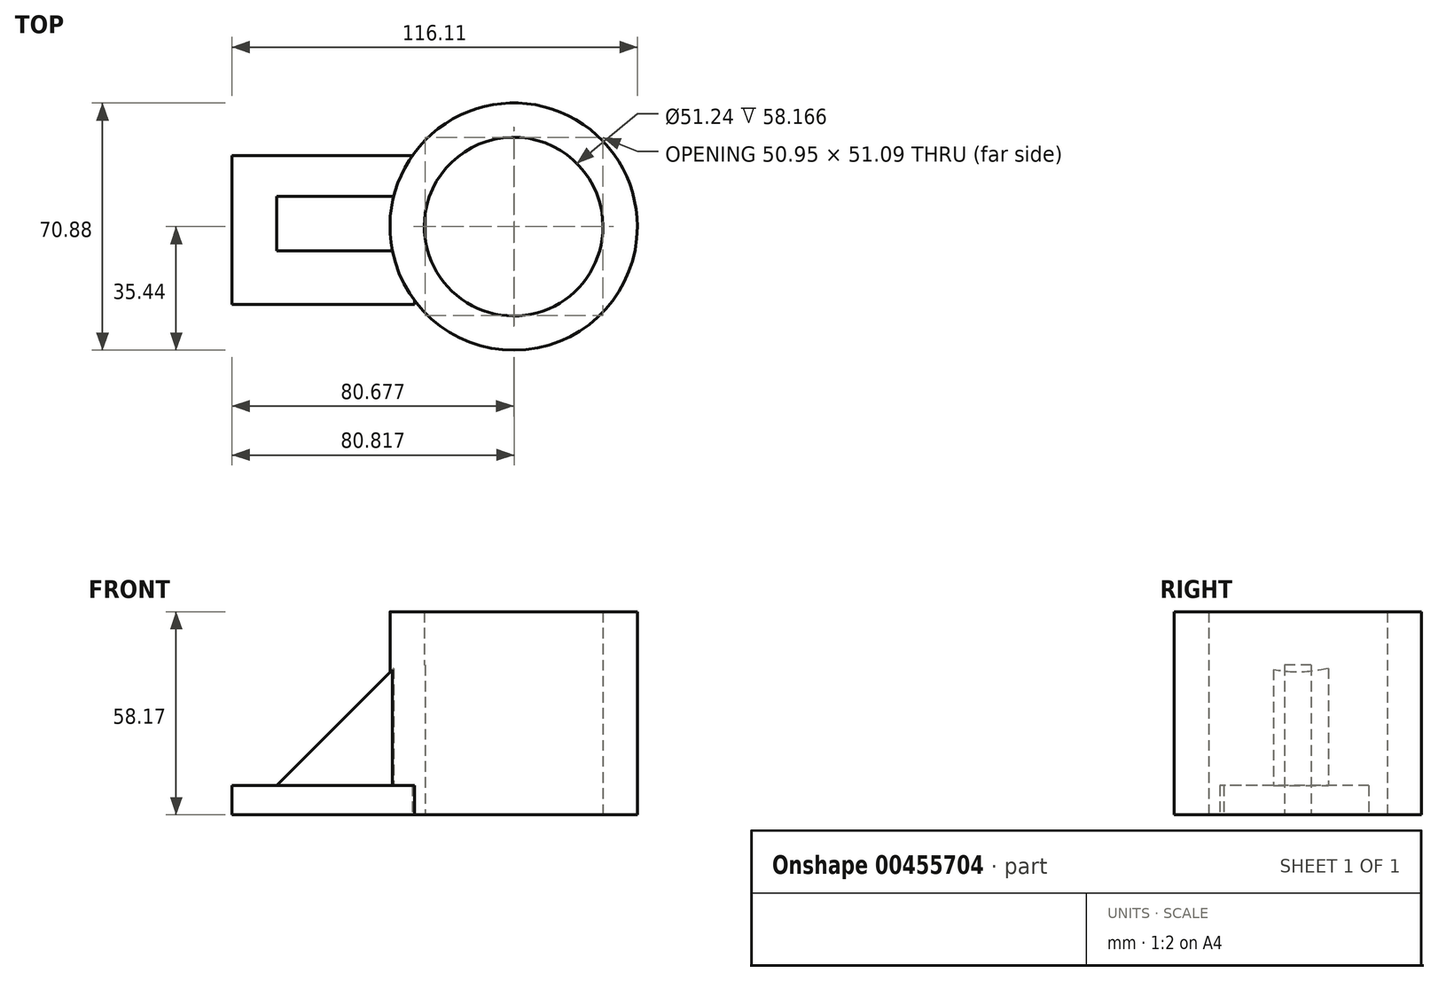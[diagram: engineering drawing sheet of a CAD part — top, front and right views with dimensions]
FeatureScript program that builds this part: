
annotation { "Feature Type Name" : "Feature", "Feature Type Description" : "" }
export const myFeature = defineFeature(function(context is Context, id is Id, definition is map)
    precondition{}
    {
        {
            var Q0;
            Q0=qCreatedBy(makeId("Top.planeOp"),FACE);
            var sketch = newSketch(context, id + "F0", { "sketchPlane" : qUnion([Q0])});
            skLineSegment(sketch, "E0.bottom", {"start": v(-55.34, 20.34) * mm, "end": v(-3, 20.34) * mm});
            skLineSegment(sketch, "E0.top", {"start": v(-55.34, -22.34) * mm, "end": v(-3, -22.34) * mm});
            skLineSegment(sketch, "E0.left", {"start": v(-55.34, 20.34) * mm, "end": v(-55.34, -22.34) * mm});
            skLineSegment(sketch, "E0.right", {"start": v(-3, 20.34) * mm, "end": v(-3, -22.34) * mm});
            skSolve(sketch);
        }
        {
            var Q0;
            Q0=makeQuery(id+"F0.imprint","IMPRINT",FACE,{"disambiguationData":[TD([[makeQuery(id+"F0.imprint","IMPRINT",EDGE,{"derivedFrom":sQuery(id+"F0.wireOp",EDGE,"E0.bottom")}),-1.0]])]});
            extrude(context, id + "F1", {"entities" : qUnion([Q0]), "depth" : 8.38 * mm});
        }
        {
            var Q0;
            Q0=qCreatedBy(makeId("Top.planeOp"),FACE);
            var sketch = newSketch(context, id + "F2", { "sketchPlane" : qUnion([Q0])});
            skCircle(sketch, "E1", {"center": v(25.34, 0) * mm, "radius": 35.44 * mm});
            skSolve(sketch);
        }
        {
            var Q0;
            Q0=makeQuery(id+"F2.imprint","IMPRINT",FACE,{"disambiguationData":[TD([[makeQuery(id+"F2.imprint","IMPRINT",EDGE,{"derivedFrom":sQuery(id+"F2.wireOp",EDGE,"E1")}),1.0]])]});
            extrude(context, id + "F3", {"entities" : qUnion([Q0]), "operationType" : NewBodyOperationType.ADD, "depth" : 58.17 * mm});
        }
        {
            var Q0;
            Q0=qCreatedBy(makeId("Top.planeOp"),FACE);
            var sketch = newSketch(context, id + "F4", { "sketchPlane" : qUnion([Q0])});
            skCircle(sketch, "E2", {"center": v(25.34, 0) * mm, "radius": 25.62 * mm});
            skSolve(sketch);
        }
        {
            var Q0;
            Q0 = qSketchRegion(id + "F4", true);
            extrude(context, id + "F5", {"entities" : qUnion([Q0]), "operationType" : NewBodyOperationType.REMOVE, "depth" : 76.45 * mm});
        }
        {
            var Q0;
            Q0=qCreatedBy(makeId("Top.planeOp"),FACE);
            var sketch = newSketch(context, id + "F6", { "sketchPlane" : qUnion([Q0])});
            skLineSegment(sketch, "E3.bottom", {"start": v(0, 8.67) * mm, "end": v(-48.67, 8.67) * mm});
            skLineSegment(sketch, "E3.top", {"start": v(0, -7) * mm, "end": v(-48.67, -7) * mm});
            skLineSegment(sketch, "E3.left", {"start": v(0, 8.67) * mm, "end": v(0, -7) * mm});
            skLineSegment(sketch, "E3.right", {"start": v(-48.67, 8.67) * mm, "end": v(-48.67, -7) * mm});
            skSolve(sketch);
        }
        {
            var Q0;
            Q0 = qSketchRegion(id + "F6", true);
            extrude(context, id + "F7", {"entities" : qUnion([Q0]), "operationType" : NewBodyOperationType.ADD, "depth" : 42.93 * mm});
        }
        {
            var Q0;
            Q0=makeQuery(id+"F7.opExtrude","CAP_EDGE",EDGE,{"disambiguationData":[OSD([sQuery(id+"F6.wireOp",EDGE,"E3.right")])],"isStart":false});
            chamfer(context, id + "F8", {"entities" : qUnion([Q0]), "width" : 40.64 * mm, "tangentPropagation" : true});
        }
    });
